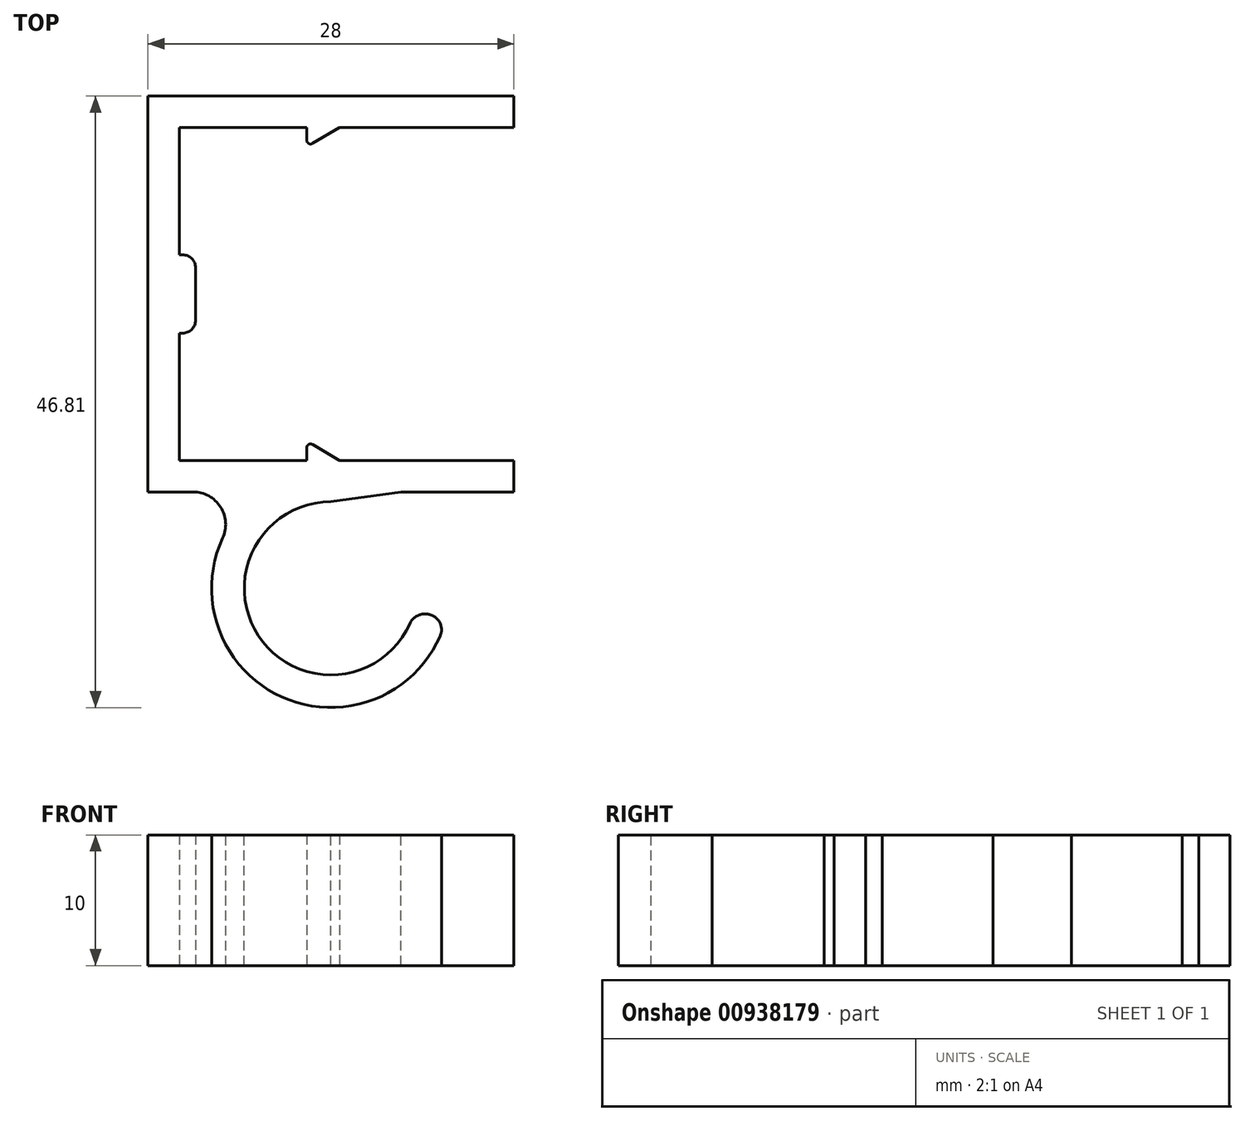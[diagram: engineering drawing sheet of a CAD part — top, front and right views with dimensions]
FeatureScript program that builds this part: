
annotation { "Feature Type Name" : "Feature", "Feature Type Description" : "" }
export const myFeature = defineFeature(function(context is Context, id is Id, definition is map)
    precondition{}
    {
        {
            var Q0;
            Q0=qCreatedBy(makeId("Top.planeOp"),FACE);
            var sketch = newSketch(context, id + "F0", { "sketchPlane" : qUnion([Q0])});
            skLineSegment(sketch, "E0.bottom", {"start": v(0, 0) * mm, "end": v(-28, 0) * mm});
            skLineSegment(sketch, "E0.top", {"start": v(0, -2.4) * mm, "end": v(-25.6, -2.4) * mm});
            skLineSegment(sketch, "E0.left", {"start": v(0, 0) * mm, "end": v(0, -2.4) * mm});
            skLineSegment(sketch, "E1.top", {"start": v(-25.6, -27.9) * mm, "end": v(0, -27.9) * mm});
            skLineSegment(sketch, "E1.right", {"start": v(0, -30.3) * mm, "end": v(0, -27.9) * mm});
            skLineSegment(sketch, "E2", {"start": v(-28, -30.3) * mm, "end": v(0, -30.3) * mm});
            skLineSegment(sketch, "E3", {"start": v(-28, -30.3) * mm, "end": v(-28, 0) * mm});
            skLineSegment(sketch, "E4", {"start": v(-25.6, -2.4) * mm, "end": v(-25.6, -27.9) * mm});
            skLineSegment(sketch, "E5.bottom", {"start": v(-25.6, -12.15) * mm, "end": v(-24.35, -12.15) * mm});
            skLineSegment(sketch, "E5.top", {"start": v(-25.6, -18.15) * mm, "end": v(-24.35, -18.15) * mm});
            skLineSegment(sketch, "E5.left", {"start": v(-25.6, -12.15) * mm, "end": v(-25.6, -18.15) * mm});
            skLineSegment(sketch, "E5.right", {"start": v(-24.35, -12.15) * mm, "end": v(-24.35, -18.15) * mm});
            skLineSegment(sketch, "E6", {"start": v(-15.85, -2.4) * mm, "end": v(-15.85, -3.9) * mm});
            skLineSegment(sketch, "E7", {"start": v(-15.85, -3.9) * mm, "end": v(-13.35, -2.4) * mm});
            skLineSegment(sketch, "E8", {"start": v(-15.85, -27.9) * mm, "end": v(-15.85, -26.4) * mm});
            skLineSegment(sketch, "E9", {"start": v(-15.85, -26.4) * mm, "end": v(-13.35, -27.9) * mm});
            skSolve(sketch);
        }
        {
            var Q0;
            Q0=qSketchRegion(id+"F0",true);
            extrude(context, id + "F1", {"entities" : qUnion([Q0]), "depth" : 10 * mm, "offsetDistance" : 25 * mm});
        }
        {
            var Q0;
            Q0=makeQuery(id+"F1.opExtrude","CAP_FACE",FACE,{"disambiguationData":[OSD([sQuery(id+"F0.wireOp",EDGE,"E0.bottom"),sQuery(id+"F0.wireOp",EDGE,"E0.top"),sQuery(id+"F0.wireOp",EDGE,"E0.left"),sQuery(id+"F0.wireOp",EDGE,"E1.top"),sQuery(id+"F0.wireOp",EDGE,"E1.right"),sQuery(id+"F0.wireOp",EDGE,"E2"),sQuery(id+"F0.wireOp",EDGE,"E3"),sQuery(id+"F0.wireOp",EDGE,"E4"),sQuery(id+"F0.wireOp",EDGE,"E5.bottom"),sQuery(id+"F0.wireOp",EDGE,"E5.top"),sQuery(id+"F0.wireOp",EDGE,"E5.right"),sQuery(id+"F0.wireOp",EDGE,"E6"),sQuery(id+"F0.wireOp",EDGE,"E7"),sQuery(id+"F0.wireOp",EDGE,"E8"),sQuery(id+"F0.wireOp",EDGE,"E9")])],"isStart":false});
            var sketch = newSketch(context, id + "F2", { "sketchPlane" : qUnion([Q0])});
            skArc(sketch, "E10", {"start": v(-14, -31.06) * mm, "mid": v(-19.33, -41.61) * mm, "end": v(-7.67, -39.65) * mm});
            skArc(sketch, "E11", {"start": v(-8.64, -30.3) * mm, "mid": v(-22.53, -40.92) * mm, "end": v(-5.09, -39.65) * mm});
            skLineSegment(sketch, "E12", {"start": v(-8.64, -30.3) * mm, "end": v(-14, -31.06) * mm});
            skLineSegment(sketch, "E13", {"start": v(-7.67, -39.65) * mm, "end": v(-5.09, -39.65) * mm});
            skCircle(sketch, "E14", {"center": v(-14, -37.68) * mm, "radius": 6.51 * mm, "construction": true});
            skSolve(sketch);
        }
        {
            var Q0;
            Q0=qSketchRegion(id+"F2",true);
            extrude(context, id + "F3", {"entities" : qUnion([Q0]), "operationType" : NewBodyOperationType.ADD, "oppositeDirection" : true, "depth" : 10 * mm, "offsetDistance" : 25 * mm});
        }
        {
            var Q0;
            Q0=makeQuery(id+"F3.opExtrude","SWEPT_EDGE",EDGE,{"disambiguationData":[OSD([sQuery(id+"F2.wireOp",EDGE,"E10"),sQuery(id+"F2.wireOp",EDGE,"E13")])]});
            var Q1;
            Q1=makeQuery(id+"F3.opExtrude","SWEPT_EDGE",EDGE,{"disambiguationData":[OSD([sQuery(id+"F2.wireOp",EDGE,"E11"),sQuery(id+"F2.wireOp",EDGE,"E13")])]});
            fillet(context, id + "F4", {"entities" : qUnion([Q0, Q1]), "radius" : 1.2 * mm, "tangentPropagation" : true, "allowEdgeOverflow" : false});
        }
        {
            var Q0;
            Q0=makeQuery(id+"F3.boolean.opBoolean","INTERSECT",EDGE,{"derivedFrom":[makeQuery(id+"F1.opExtrude","SWEPT_FACE",FACE,{"disambiguationData":[OSD([sQuery(id+"F0.wireOp",EDGE,"E2")])]}),makeQuery(id+"F3.opExtrude","SWEPT_FACE",FACE,{"disambiguationData":[OSD([sQuery(id+"F2.wireOp",EDGE,"E11")])]})]});
            fillet(context, id + "F5", {"entities" : qUnion([Q0]), "radius" : 2.5 * mm, "tangentPropagation" : true, "allowEdgeOverflow" : false});
        }
        {
            var Q0;
            Q0=makeQuery(id+"F1.opExtrude","SWEPT_EDGE",EDGE,{"disambiguationData":[OSD([sQuery(id+"F0.wireOp",EDGE,"E5.bottom"),sQuery(id+"F0.wireOp",EDGE,"E5.right")])]});
            var Q1;
            Q1=makeQuery(id+"F1.opExtrude","SWEPT_EDGE",EDGE,{"disambiguationData":[OSD([sQuery(id+"F0.wireOp",EDGE,"E5.top"),sQuery(id+"F0.wireOp",EDGE,"E5.right")])]});
            fillet(context, id + "F6", {"entities" : qUnion([Q0, Q1]), "radius" : 1 * mm, "tangentPropagation" : true, "allowEdgeOverflow" : false});
        }
        {
            var Q0;
            Q0=makeQuery(id+"F1.opExtrude","SWEPT_EDGE",EDGE,{"disambiguationData":[OSD([sQuery(id+"F0.wireOp",EDGE,"E6"),sQuery(id+"F0.wireOp",EDGE,"E7")])]});
            var Q1;
            Q1=makeQuery(id+"F1.opExtrude","SWEPT_EDGE",EDGE,{"disambiguationData":[OSD([sQuery(id+"F0.wireOp",EDGE,"E8"),sQuery(id+"F0.wireOp",EDGE,"E9")])]});
            fillet(context, id + "F7", {"entities" : qUnion([Q0, Q1]), "radius" : .3 * mm, "tangentPropagation" : true, "allowEdgeOverflow" : false});
        }
    });
